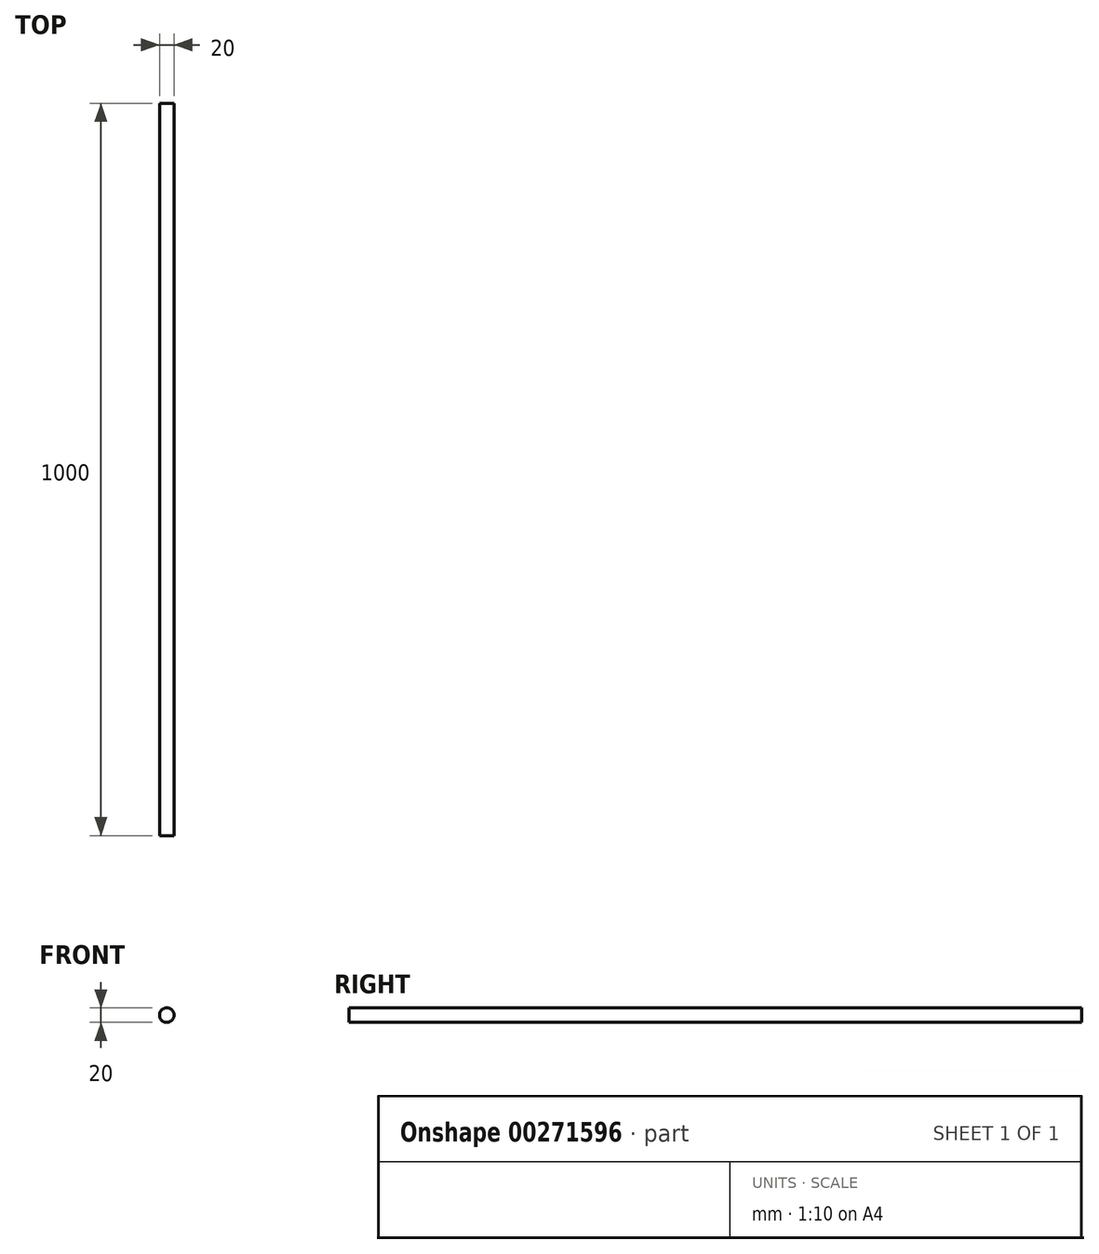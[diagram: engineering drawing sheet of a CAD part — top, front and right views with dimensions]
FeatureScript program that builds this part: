
annotation { "Feature Type Name" : "Feature", "Feature Type Description" : "" }
export const myFeature = defineFeature(function(context is Context, id is Id, definition is map)
    precondition{}
    {
        {
            var Q0;
            Q0=qCreatedBy(makeId("Front.planeOp"),FACE);
            var sketch = newSketch(context, id + "F0", { "sketchPlane" : qUnion([Q0])});
            skCircle(sketch, "E0", {"center": v(0, 0) * mm, "radius": 10 * mm});
            skSolve(sketch);
        }
        {
            var Q0;
            Q0 = qSketchRegion(id + "F0", true);
            extrude(context, id + "F1", {"entities" : qUnion([Q0]), "depth" : 1000 * mm});
        }
    });
